# Revit family: IS_ConnectAir_E0137_BIM_DE
name_source: partatom
category: Plumbing Fixtures
revit_build: Autodesk Revit MEP 2014 (Build: 20130308_1515(x64)
units: mm (PartAtom-declared; Revit-internal decimal feet)

## types (2) — shared parameters
Accessories = www.idealstandard.de\ersatzteile
AreaUnits = millimeters
Assembly Code = C1030200
AssetType = Fixed
Brand = Ideal Standard
CodePerformance = DIN EN 997, CL1-6-VRII, DIN EN 33
ConnectionType = Plumbing
DurationUnit = year
ExpectedLife = 25
Features = Connect Air compact close coupled back-to-wall bowl, wash-down, AquaBlade
GrossWeight = 0
IfcExportAs = IfcSanitaryTerminalType
IfcExportType = TOILETPAN
InstallationInstructions = www.idealstandard.de\produkte
LinearUnits = millimeters
ManufacturerURL = www.idealstandard.com
NBSDescription = WC pans
NBSReference = 45-30-70/384
NettWeight = 32,7 kg
NominalHeight = 400 mm  [stored 1.31234 ft]
NominalLength = 659 mm
NominalWidth = 360 mm
PanColor = White
PanMaterial = Vitreous china
PanMounting = BackToWall
ProductInformation = www.idealstandard.de/produkte
Shape = Sculptured
Size = 360x660x780mm
Space = Internal
ToiletPanType = WashDown
ToiletType = Other
URL = www.idealstandard.com
Uniclass2015Code = Pr_40_20_93_94
Uniclass2015Title = WC pans
Uniclass2015Version = Products v1.1
Version = 1
VolumeUnits = Litres
WarrantyDescription = Manufacturers Warranty
WarrantyDurationUnit = year
zero-valued in all types: CWFU, Cost, Default Elevation, HWFU, SpilloverLevel, WFU

## per-type parameters (varying)
| type | BIMObjectName | BarCode | Description | Finish | Model | ModelNumber | ModelReference | Name |
| E013701 - Connect Air compact close coupled back-to-wall bowl, wash-down, AquaBlade | ISI_IdealStandard_WcPans_ConnectAir_E013701 | 5017830514237 | E013701 Connect Air compact close coupled back-to-wall bowl, wash-down, AquaBlade | white | E013701 | E013701 | E013701 Connect Air compact close coupled back-to-wall bowl, wash-down, AquaBlade | WcPans_ConnectAir_E013701_IdealStandard |
| E0137MA - Connect Air compact close coupled back-to-wall bowl, wash-down, AquaBlade | ISI_IdealStandard_WcPans_ConnectAir_E0137MA | 5017830518280 | E0137MA Connect Air compact close coupled back-to-wall bowl, wash-down, AquaBlade | white with ideal plus | E0137MA | E0137MA | E0137MA Connect Air compact close coupled back-to-wall bowl, wash-down, AquaBlade | WcPans_ConnectAir_E0137MA_IdealStandard |

note: [stored X ft] marks values corroborated as IEEE doubles in the binary element streams (Revit-internal decimal feet)

## geometry (parser evidence)
native form markers: Sweep x9
no freeform markers — native parametric forms only
